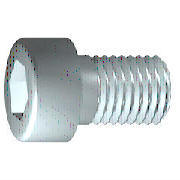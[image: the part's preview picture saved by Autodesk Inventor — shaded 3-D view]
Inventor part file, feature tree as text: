
AUTODESK INVENTOR PART (.ipt)
format: ipt  version: 2022 (Build 260153000, 153)  size: 192,512 bytes
history: native  units: mm (DEFAULTED — no unit token found)
features: sketch x2, extrude x1, plane x1, fillet x1
ambient origin geometry x7: Origin, YZ Plane, XY Plane, X Axis, Y Axis, Z Axis, Center Point
bodies: Solid1 (feature_tree), Body (feature_tree)
feature tree (5):
  extrude  "Slot"  Depth=6.0mm
  plane  "Work Plane1"
  fillet  "Fillet2"  Radius=6.0mm
  sketch  "Sketch1"  dims[d1=22.5mm d2=0.61355mm d3=6.0mm]
  sketch  "Sketch2"  dims[d4=3.0mm d5=60.0deg d6=6.0mm d7=6.0mm d8=5.773503mm d9=10.0mm d10=90.0deg d11=10.0mm d12=0.0mm d13=22.5mm d14=0.0mm d15=0.61345mm d16=0.61345mm d17=0.6mm d19=0.0mm d26=25.0mm d27=45.0deg d28=0.0mm d29=0.0mm d30=0.1mm]
